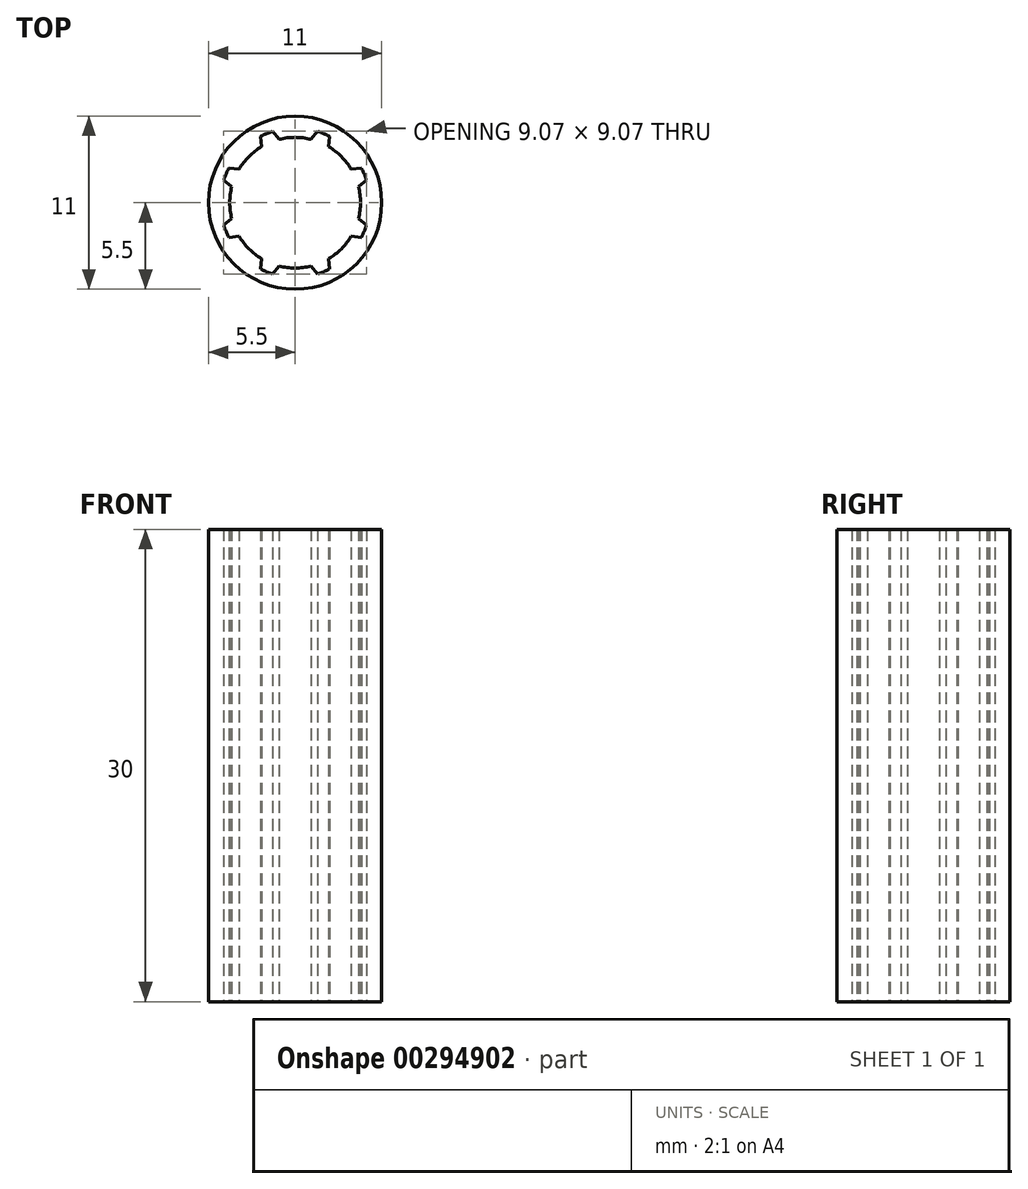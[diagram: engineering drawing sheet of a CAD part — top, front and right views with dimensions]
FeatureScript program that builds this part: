
annotation { "Feature Type Name" : "Feature", "Feature Type Description" : "" }
export const myFeature = defineFeature(function(context is Context, id is Id, definition is map)
    precondition{}
    {
        {
            var Q0;
            Q0=qCreatedBy(makeId("Top.planeOp"),FACE);
            var sketch = newSketch(context, id + "F0", { "sketchPlane" : qUnion([Q0])});
            skCircle(sketch, "E0", {"center": v(0, 0) * mm, "radius": 5.5 * mm});
            skCircle(sketch, "E1", {"center": v(0, 0) * mm, "radius": 4.75 * mm});
            skPoint(sketch, "E2", {"position": v(-1.42, 4.53) * mm});
            skPoint(sketch, "E3", {"position": v(-1.02, 4.02) * mm});
            skPoint(sketch, "E4", {"position": v(1.02, 4.02) * mm});
            skLineSegment(sketch, "E5", {"start": v(-1.42, 4.53) * mm, "end": v(-1.02, 4.02) * mm});
            skPoint(sketch, "E6", {"position": v(1.42, 4.53) * mm});
            skLineSegment(sketch, "E7", {"start": v(1.02, 4.02) * mm, "end": v(1.42, 4.53) * mm});
            skArc(sketch, "E8", {"start": v(-1.02, 4.02) * mm, "mid": v(0, 4.15) * mm, "end": v(1.02, 4.02) * mm});
            skLineSegment(sketch, "E9.1.0", {"start": v(-2.13, 3.56) * mm, "end": v(-2.2, 4.2) * mm});
            skArc(sketch, "E9.1.1", {"start": v(-3.56, 2.13) * mm, "mid": v(-2.93, 2.93) * mm, "end": v(-2.13, 3.56) * mm});
            skLineSegment(sketch, "E9.1.2", {"start": v(-4.2, 2.2) * mm, "end": v(-3.56, 2.13) * mm});
            skLineSegment(sketch, "E9.2.0", {"start": v(-4.02, 1.02) * mm, "end": v(-4.53, 1.42) * mm});
            skArc(sketch, "E9.2.1", {"start": v(-4.02, -1.02) * mm, "mid": v(-4.15, 0) * mm, "end": v(-4.02, 1.02) * mm});
            skLineSegment(sketch, "E9.2.2", {"start": v(-4.53, -1.42) * mm, "end": v(-4.02, -1.02) * mm});
            skLineSegment(sketch, "E9.3.0", {"start": v(-3.56, -2.13) * mm, "end": v(-4.2, -2.2) * mm});
            skArc(sketch, "E9.3.1", {"start": v(-2.13, -3.56) * mm, "mid": v(-2.93, -2.93) * mm, "end": v(-3.56, -2.13) * mm});
            skLineSegment(sketch, "E9.3.2", {"start": v(-2.2, -4.2) * mm, "end": v(-2.13, -3.56) * mm});
            skLineSegment(sketch, "E9.4.0", {"start": v(-1.02, -4.02) * mm, "end": v(-1.42, -4.53) * mm});
            skArc(sketch, "E9.4.1", {"start": v(1.02, -4.02) * mm, "mid": v(0, -4.15) * mm, "end": v(-1.02, -4.02) * mm});
            skLineSegment(sketch, "E9.4.2", {"start": v(1.42, -4.53) * mm, "end": v(1.02, -4.02) * mm});
            skLineSegment(sketch, "E9.5.0", {"start": v(2.13, -3.56) * mm, "end": v(2.2, -4.2) * mm});
            skArc(sketch, "E9.5.1", {"start": v(3.56, -2.13) * mm, "mid": v(2.93, -2.93) * mm, "end": v(2.13, -3.56) * mm});
            skLineSegment(sketch, "E9.5.2", {"start": v(4.2, -2.2) * mm, "end": v(3.56, -2.13) * mm});
            skLineSegment(sketch, "E9.6.0", {"start": v(4.02, -1.02) * mm, "end": v(4.53, -1.42) * mm});
            skArc(sketch, "E9.6.1", {"start": v(4.02, 1.02) * mm, "mid": v(4.15, 0) * mm, "end": v(4.02, -1.02) * mm});
            skLineSegment(sketch, "E9.6.2", {"start": v(4.53, 1.42) * mm, "end": v(4.02, 1.02) * mm});
            skLineSegment(sketch, "E9.7.0", {"start": v(3.56, 2.13) * mm, "end": v(4.2, 2.2) * mm});
            skArc(sketch, "E9.7.1", {"start": v(2.13, 3.56) * mm, "mid": v(2.93, 2.93) * mm, "end": v(3.56, 2.13) * mm});
            skLineSegment(sketch, "E9.7.2", {"start": v(2.2, 4.2) * mm, "end": v(2.13, 3.56) * mm});
            skSolve(sketch);
        }
        {
            var Q0;
            Q0=makeQuery(id+"F0.imprint","IMPRINT",FACE,{"disambiguationData":[TD([[makeQuery(id+"F0.imprint","IMPRINT",EDGE,{"derivedFrom":sQuery(id+"F0.wireOp",EDGE,"E0")}),1.0]])]});
            var Q1;
            {var subQ0=sQuery(id+"F0.wireOp",EDGE,"E9.2.0");Q1=makeQuery(id+"F0.imprint","IMPRINT",FACE,{"disambiguationData":[TD([[makeQuery(id+"F0.imprint","IMPRINT",EDGE,{"derivedFrom":subQ0}),1.0]])]});}
            var Q2;
            {var subQ0=sQuery(id+"F0.wireOp",EDGE,"E9.1.0");Q2=makeQuery(id+"F0.imprint","IMPRINT",FACE,{"disambiguationData":[TD([[makeQuery(id+"F0.imprint","IMPRINT",EDGE,{"derivedFrom":subQ0}),1.0]])]});}
            var Q3;
            {var subQ0=sQuery(id+"F0.wireOp",EDGE,"E5");Q3=makeQuery(id+"F0.imprint","IMPRINT",FACE,{"disambiguationData":[TD([[makeQuery(id+"F0.imprint","IMPRINT",EDGE,{"derivedFrom":subQ0}),1.0]])]});}
            var Q4;
            {var subQ0=sQuery(id+"F0.wireOp",EDGE,"E9.7.0");Q4=makeQuery(id+"F0.imprint","IMPRINT",FACE,{"disambiguationData":[TD([[makeQuery(id+"F0.imprint","IMPRINT",EDGE,{"derivedFrom":subQ0}),1.0]])]});}
            var Q5;
            {var subQ0=sQuery(id+"F0.wireOp",EDGE,"E9.6.0");Q5=makeQuery(id+"F0.imprint","IMPRINT",FACE,{"disambiguationData":[TD([[makeQuery(id+"F0.imprint","IMPRINT",EDGE,{"derivedFrom":subQ0}),1.0]])]});}
            var Q6;
            {var subQ0=sQuery(id+"F0.wireOp",EDGE,"E9.5.0");Q6=makeQuery(id+"F0.imprint","IMPRINT",FACE,{"disambiguationData":[TD([[makeQuery(id+"F0.imprint","IMPRINT",EDGE,{"derivedFrom":subQ0}),1.0]])]});}
            var Q7;
            {var subQ0=sQuery(id+"F0.wireOp",EDGE,"E9.4.0");Q7=makeQuery(id+"F0.imprint","IMPRINT",FACE,{"disambiguationData":[TD([[makeQuery(id+"F0.imprint","IMPRINT",EDGE,{"derivedFrom":subQ0}),1.0]])]});}
            var Q8;
            {var subQ0=sQuery(id+"F0.wireOp",EDGE,"E9.3.0");Q8=makeQuery(id+"F0.imprint","IMPRINT",FACE,{"disambiguationData":[TD([[makeQuery(id+"F0.imprint","IMPRINT",EDGE,{"derivedFrom":subQ0}),1.0]])]});}
            extrude(context, id + "F1", {"entities" : qUnion([Q0, Q1, Q2, Q3, Q4, Q5, Q6, Q7, Q8]), "depth" : 30 * mm});
        }
    });
